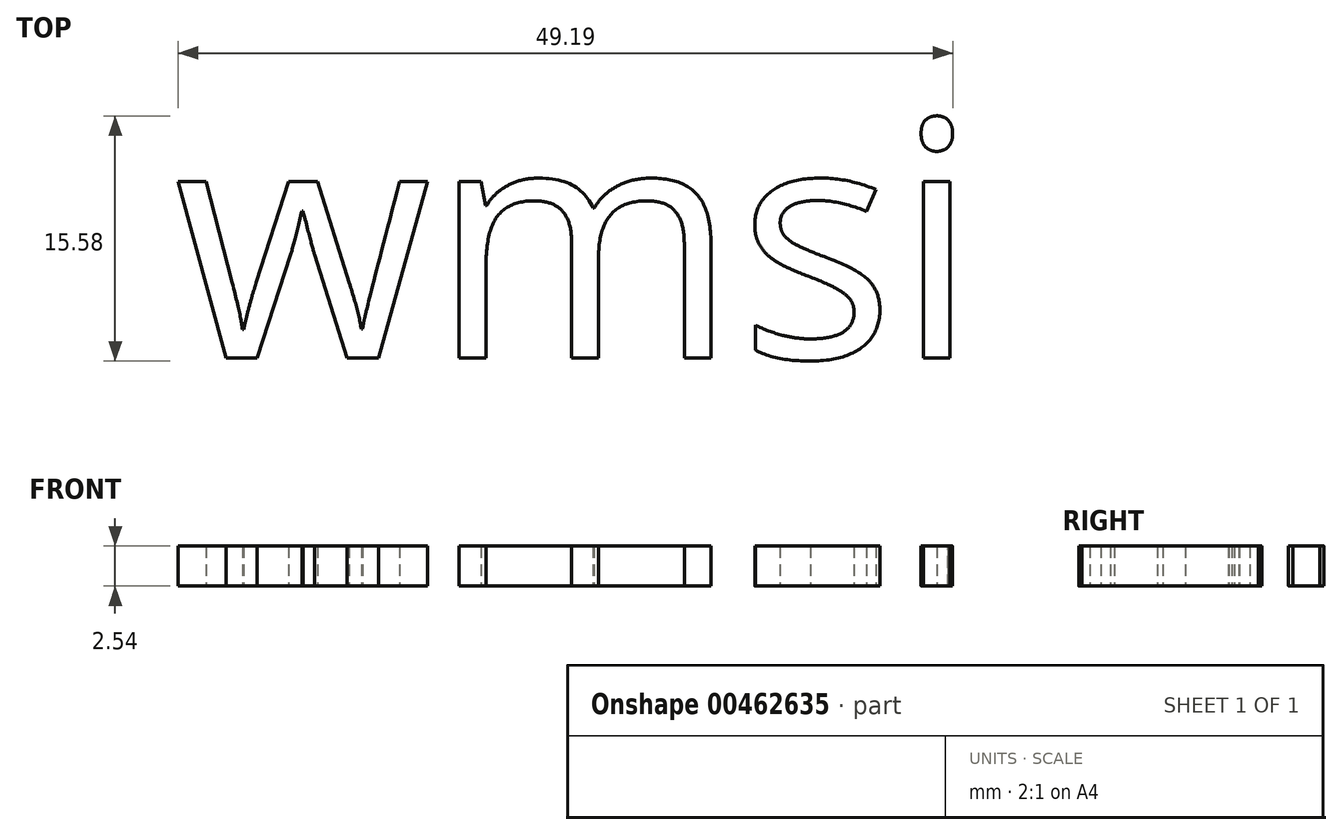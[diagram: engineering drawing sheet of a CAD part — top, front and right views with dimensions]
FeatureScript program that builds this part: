
annotation { "Feature Type Name" : "Feature", "Feature Type Description" : "" }
export const myFeature = defineFeature(function(context is Context, id is Id, definition is map)
    precondition{}
    {
        {
            var Q0;
            Q0=qCreatedBy(makeId("Top.planeOp"),FACE);
            var sketch = newSketch(context, id + "F0", { "sketchPlane" : qUnion([Q0])});
            skText(sketch, "E0", { "text": "wmsi", "fontName": "OpenSans-Regular.ttf"});
            const initialGuessF0  = {"E0": [-0.0508, 0, 1, 0, 0.01508]};
            skSetInitialGuess(sketch, initialGuessF0);
            skSolve(sketch);
        }
        {
            var Q0;
            Q0 = qSketchRegion(id + "F0", true);
            extrude(context, id + "F1", {"entities" : qUnion([Q0]), "depth" : 2.54 * mm});
        }
    });
